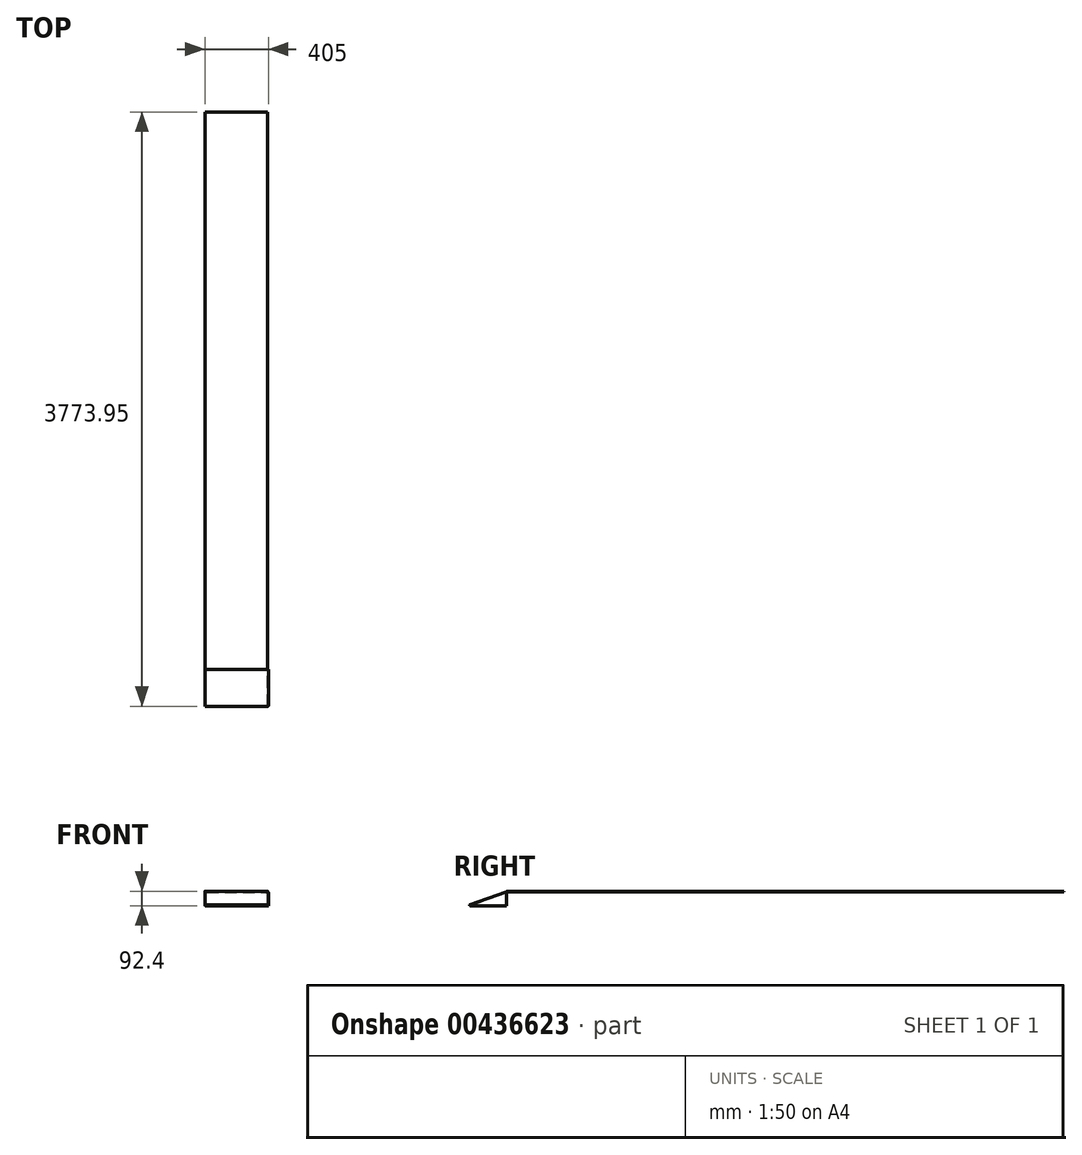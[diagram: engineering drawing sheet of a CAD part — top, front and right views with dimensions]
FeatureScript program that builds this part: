
annotation { "Feature Type Name" : "Feature", "Feature Type Description" : "" }
export const myFeature = defineFeature(function(context is Context, id is Id, definition is map)
    precondition{}
    {
        {
            var Q0;
            Q0=qCreatedBy(makeId("Top.planeOp"),FACE);
            var sketch = newSketch(context, id + "F0", { "sketchPlane" : qUnion([Q0])});
            skLineSegment(sketch, "E0.bottom", {"start": v(200, 1765) * mm, "end": v(-200, 1765) * mm});
            skLineSegment(sketch, "E0.top", {"start": v(200, -1765) * mm, "end": v(-200, -1765) * mm});
            skLineSegment(sketch, "E0.left", {"start": v(200, 1765) * mm, "end": v(200, -1765) * mm});
            skLineSegment(sketch, "E0.right", {"start": v(-200, 1765) * mm, "end": v(-200, -1765) * mm});
            skPoint(sketch, "E0.middle", {"position": v(0, 0) * mm});
            skSolve(sketch);
        }
        {
            var Q0;
            Q0 = qSketchRegion(id + "F0", true);
            extrude(context, id + "F1", {"entities" : qUnion([Q0]), "depth" : 5 * mm});
        }
        {
            var Q0;
            Q0=makeQuery(id+"F1.opExtrude","SWEPT_FACE",FACE,{"disambiguationData":[OSD([sQuery(id+"F0.wireOp",EDGE,"E0.left")])]});
            var sketch = newSketch(context, id + "F2", { "sketchPlane" : qUnion([Q0])});
            skLineSegment(sketch, "E1", {"start": v(-1765, 5) * mm, "end": v(-1765, 0) * mm});
            skArc(sketch, "E2", {"start": v(-1765, 0) * mm, "mid": v(-1768.77, -0.48) * mm, "end": v(-1772.3, -1.9) * mm});
            skLineSegment(sketch, "E3", {"start": v(-1772.3, -1.9) * mm, "end": v(-1774.03, 2.85) * mm});
            skArc(sketch, "E4", {"start": v(-1765, 5) * mm, "mid": v(-1769.64, 4.45) * mm, "end": v(-1774.03, 2.85) * mm});
            skPoint(sketch, "E5.orphan", {"position": v(-1772.99, 0) * mm});
            skSolve(sketch);
        }
        {
            var Q0;
            Q0 = qSketchRegion(id + "F2", true);
            var Q1;
            Q1=makeQuery(id+"F1.opExtrude","SWEPT_FACE",FACE,{"disambiguationData":[OSD([sQuery(id+"F0.wireOp",EDGE,"E0.right")])]});
            extrude(context, id + "F3", {"entities" : qUnion([Q0]), "operationType" : NewBodyOperationType.ADD, "endBound" : BoundingType.UP_TO_SURFACE, "oppositeDirection" : true, "endBoundEntityFace" : qUnion([Q1]), "depth" : 25 * mm});
        }
        {
            var Q0;
            Q0=makeQuery(id+"F3.opExtrude","SWEPT_FACE",FACE,{"disambiguationData":[OSD([sQuery(id+"F2.wireOp",EDGE,"E3")])]});
            extrude(context, id + "F4", {"entities" : qUnion([Q0]), "operationType" : NewBodyOperationType.ADD, "depth" : 250 * mm});
        }
        {
            var Q0;
            Q0=makeQuery(id+"F4.opExtrude","SWEPT_FACE",FACE,{"disambiguationData":[OSD([sQuery(id+"F2.wireOp",EDGE,"E3"),sQuery(id+"F2.wireOp",EDGE,"E4")])]});
            var sketch = newSketch(context, id + "F5", { "sketchPlane" : qUnion([Q0])});
            skLineSegment(sketch, "E6", {"start": v(200, -1666.07) * mm, "end": v(188, -1666.07) * mm});
            skLineSegment(sketch, "E7", {"start": v(187.5, -1666.57) * mm, "end": v(187.5, -1667.57) * mm});
            skLineSegment(sketch, "E8", {"start": v(188, -1668.07) * mm, "end": v(200, -1668.07) * mm});
            skLineSegment(sketch, "E9", {"start": v(200, -1668.07) * mm, "end": v(200, -1666.07) * mm});
            skPoint(sketch, "E10.visualSharp", {"position": v(187.5, -1668.07) * mm});
            skArc(sketch, "E10.filletArc", {"start": v(187.5, -1667.57) * mm, "mid": v(187.65, -1667.92) * mm, "end": v(188, -1668.07) * mm});
            skPoint(sketch, "E11.visualSharp", {"position": v(187.5, -1666.07) * mm});
            skArc(sketch, "E11.filletArc", {"start": v(188, -1666.07) * mm, "mid": v(187.65, -1666.21) * mm, "end": v(187.5, -1666.57) * mm});
            skLineSegment(sketch, "E12", {"start": v(0, -1916.07) * mm, "end": v(0, -1666.07) * mm, "construction": true});
            skArc(sketch, "E13.MirrorCS", {"start": v(-187.5, -1667.57) * mm, "mid": v(-187.65, -1667.92) * mm, "end": v(-188, -1668.07) * mm});
            skLineSegment(sketch, "E14.MirrorCS", {"start": v(-187.5, -1666.57) * mm, "end": v(-187.5, -1667.57) * mm});
            skArc(sketch, "E15.MirrorCS", {"start": v(-188, -1666.07) * mm, "mid": v(-187.65, -1666.21) * mm, "end": v(-187.5, -1666.57) * mm});
            skLineSegment(sketch, "E16.MirrorCS", {"start": v(-200, -1666.07) * mm, "end": v(-188, -1666.07) * mm});
            skLineSegment(sketch, "E17.MirrorCS", {"start": v(-188, -1668.07) * mm, "end": v(-200, -1668.07) * mm});
            skLineSegment(sketch, "E18.MirrorCS", {"start": v(-200, -1668.07) * mm, "end": v(-200, -1666.07) * mm});
            skPoint(sketch, "E19.MirrorP", {"position": v(-187.5, -1668.07) * mm});
            skPoint(sketch, "E20.MirrorP", {"position": v(-187.5, -1666.07) * mm});
            skSolve(sketch);
        }
        {
            var Q0;
            Q0 = qSketchRegion(id + "F5", true);
            extrude(context, id + "F6", {"entities" : qUnion([Q0]), "operationType" : NewBodyOperationType.REMOVE, "endBound" : BoundingType.THROUGH_ALL, "oppositeDirection" : true, "depth" : 25 * mm});
        }
        {
            var Q0;
            {var subQ0=sQuery(id+"F2.wireOp",EDGE,"E3");var subQ1=sQuery(id+"F2.wireOp",EDGE,"E2");var subQ2=sQuery(id+"F2.wireOp",EDGE,"E4");Q0=makeQuery(id+"F6.boolean.opBoolean","SPLIT",FACE,{"disambiguationData":[TD([makeQuery(id+"F4.opExtrude","CAP_FACE",FACE,{"disambiguationData":[OSD([subQ0])],"isStart":false})])],"derivedFrom":makeQuery(id+"F4.boolean.opBoolean","MERGE",FACE,{"derivedFrom":[makeQuery(id+"F3.boolean.opBoolean","MERGE",FACE,{"derivedFrom":[makeQuery(id+"F1.opExtrude","SWEPT_FACE",FACE,{"disambiguationData":[OSD([sQuery(id+"F0.wireOp",EDGE,"E0.left")])]}),makeQuery(id+"F3.opExtrude","CAP_FACE",FACE,{"disambiguationData":[OSD([sQuery(id+"F2.wireOp",EDGE,"E1"),subQ1,subQ0,subQ2])],"isStart":true})]}),makeQuery(id+"F4.opExtrude","SWEPT_FACE",FACE,{"disambiguationData":[OSD([subQ0])]})]})});}
            var sketch = newSketch(context, id + "F7", { "sketchPlane" : qUnion([Q0])});
            skLineSegment(sketch, "E21", {"start": v(-2008.95, -82.66) * mm, "end": v(-1775.9, 2.16) * mm});
            skLineSegment(sketch, "E22", {"start": v(-1775.9, 2.16) * mm, "end": v(-1774.18, -2.58) * mm});
            skLineSegment(sketch, "E23", {"start": v(-1774.18, -2.58) * mm, "end": v(-1774.18, -87.4) * mm});
            skLineSegment(sketch, "E24", {"start": v(-1774.18, -87.4) * mm, "end": v(-2007.22, -87.4) * mm});
            skLineSegment(sketch, "E25", {"start": v(-2007.22, -87.4) * mm, "end": v(-2008.95, -82.66) * mm});
            skSolve(sketch);
        }
        {
            var Q0;
            Q0 = qSketchRegion(id + "F7", true);
            extrude(context, id + "F8", {"entities" : qUnion([Q0]), "operationType" : NewBodyOperationType.ADD, "depth" : 5 * mm});
        }
        {
            var Q0;
            Q0=makeQuery(id+"F8.opExtrude","CAP_EDGE",EDGE,{"disambiguationData":[OSD([sQuery(id+"F7.wireOp",EDGE,"E21")])],"isStart":false});
            fillet(context, id + "F9", {"entities" : qUnion([Q0]), "radius" : 10 * mm, "tangentPropagation" : true, "allowEdgeOverflow" : false});
        }
        {
            var Q0;
            Q0=makeQuery(id+"F4.opExtrude","SWEPT_EDGE",EDGE,{"disambiguationData":[OSD([sQuery(id+"F2.wireOp",EDGE,"E2"),sQuery(id+"F2.wireOp",EDGE,"E3")])]});
            fillet(context, id + "F10", {"entities" : qUnion([Q0]), "radius" : 5 * mm, "tangentPropagation" : true, "allowEdgeOverflow" : false});
        }
    });
